# Revit family: Plumbing-Valves-Sloan-ROYAL-110-ESS
name_source: partatom
category: Plumbing Fixtures
units: mm (PartAtom-declared; Revit-internal decimal feet)

## family parameters
Cut with Voids When Loaded = No
Host = Face
OmniClass Number = 23.45.05.14.99
OmniClass Title = Other Sanitary Washing Plumbing Fixtures
Part Type = Normal
Room Calculation Point = No
Round Connector Dimension = Use Diameter
Shared = No

## types (6) — shared parameters
Apparent Load = 0 VA
Assembly Code = D2020300
CW Connection = Yes
Centerline of Supply from Top of Fixture = 11 1/2"
Centerline of Supply to Centerline of Valve = 4 3/4"
Current = 0 A
Default Elevation = 0"
Edition number = 1
Flush Rate = 3.5 gpf (13.2 Lpf)
HW Connection = No
Height = 13 5/8"
Keynote = 15410
Manufacturer = Sloan Valve
Number of Poles = 3
Operating Water Pressure = 15 – 80 PSI (103 – 552 kPa)
Power Factor = 0.8
Product Material = Sloan Valve - Finish - Polished Chrome
Product data url = https://bimobject.com
URL = www.sloanvalve.com
Valve Pressure Drop = 0.00 psi
Vent Connection = No
Voltage = 24 V
Waste Connection = No
Water Inlet Connection Diameter = 1"
zero-valued in all types: CWFU, HWFU, WFU

## per-type parameters (varying)
| type | Description | Part Number | z_Electrical Box |
| ROYAL 110 ESS-3.5-OR-HW | 3.5 gpf, Polished Chrome Finish, Fixture Connection Top Spud, Single Flush, Electrical Override, Hardwired, Sensor-Operated, Royal® Exposed Sensor Hardwired Water Closet Flushometer. | 3450147 | Yes |
| ROYAL 110 ESS-3.5-TMO-HW | 3.5 gpf, Polished Chrome Finish, Fixture Connection Top Spud, Single Flush, True Mechanical Override, Hardwired, Sensor-Operated, Royal® Exposed Sensor Hardwired Water Closet Flushometer. | 3450155 | No |
| ROYAL 110 ESS-3.5-YG-OR-TP-HW | 3.5 gpf, Angle Stop Extended Bumper, Polished Chrome Finish, Fixture Connection Top Spud, Single Flush, Trap Primer Outlet Tube, Electrical Override, Hardwired, Sensor-Operated, Royal® Exposed Sensor Hardwired Water Closet Flushometer. | 3450110 | Yes |
| ROYAL 110 ESS-3.5-YO-OR-HW | 3.5 gpf, Angle Stop Bumper, Polished Chrome Finish, Fixture Connection Top Spud, Single Flush, Electrical Override, Hardwired, Sensor-Operated, Royal® Exposed Sensor Hardwired Water Closet Flushometer. | 3910120 | Yes |
| ROYAL 110 ESS-3.5-OR-YK-HW | 3.5 gpf, Polished Chrome Finish, Fixture Connection Top Spud, Single Flush, Electrical Override, Solid Ring Pipe Support, Hardwired, SensorOperated, Royal® Exposed Sensor Hardwired Water Closet Flushometer. | 3910237 | Yes |
| ROYAL 110 ESS-3.5-YG-OR-HW | 3.5 gpf, Angle Stop Extended Bumper, Polished Chrome Finish, Fixture Connection Top Spud, Single Flush, Electrical Override, Hardwired, Sensor-Operated, Royal® Exposed Sensor Hardwired Water Closet Flushometer. | 3450108 | Yes |

note: column(s) folded — value = type name in every type: Model

## geometry (parser evidence)
native form markers: Sweep x6
no freeform markers — native parametric forms only
